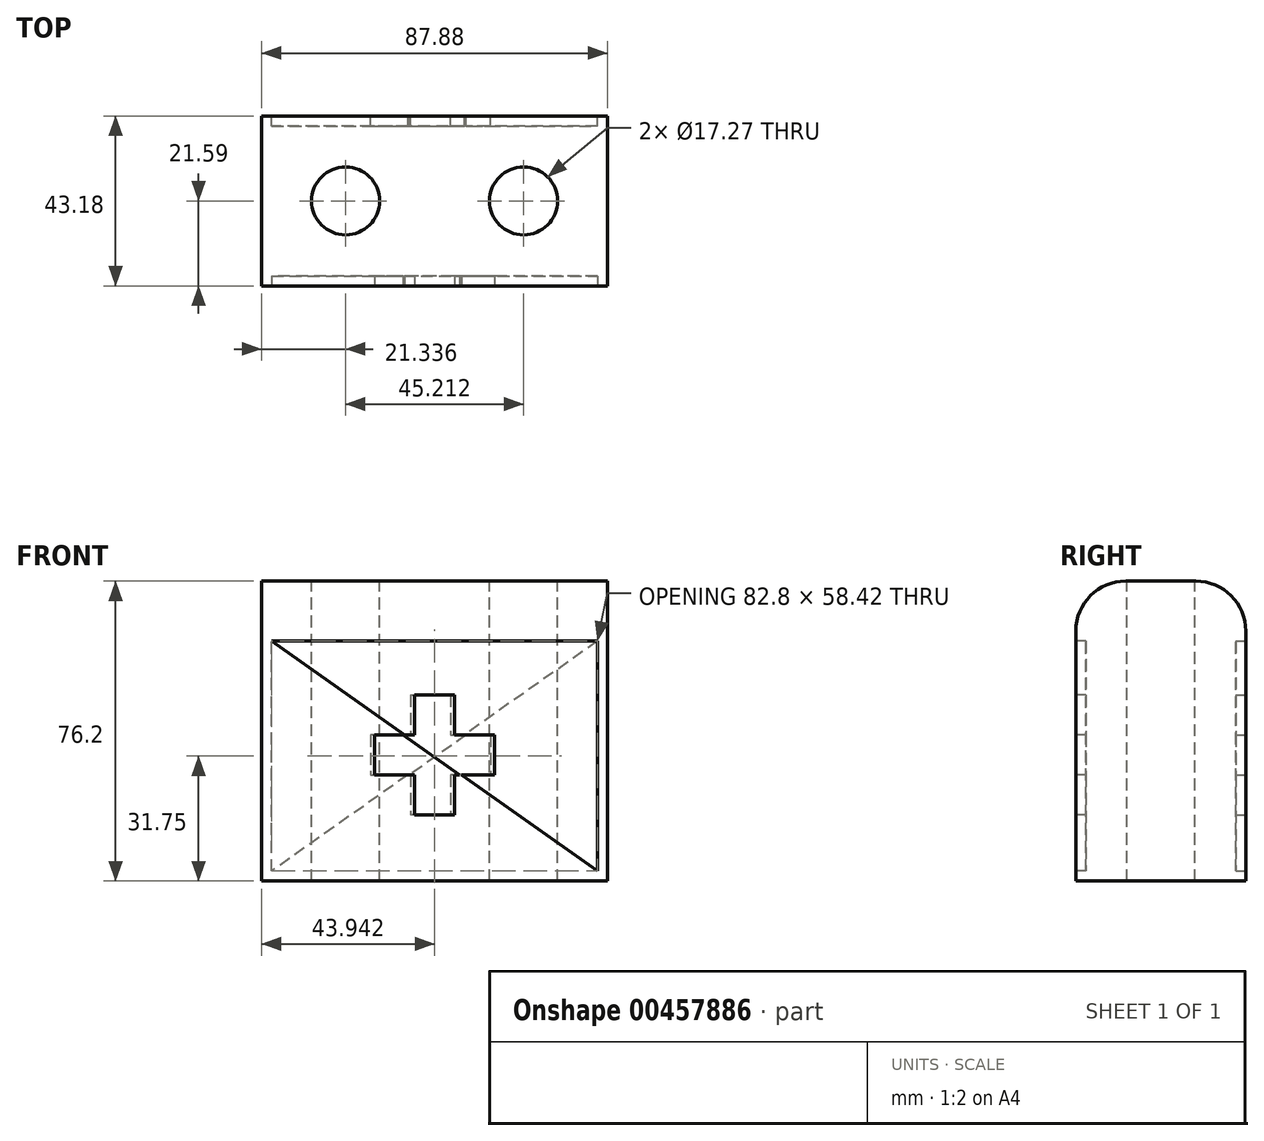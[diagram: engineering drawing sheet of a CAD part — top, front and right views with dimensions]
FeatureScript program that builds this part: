
annotation { "Feature Type Name" : "Feature", "Feature Type Description" : "" }
export const myFeature = defineFeature(function(context is Context, id is Id, definition is map)
    precondition{}
    {
        {
            var Q0;
            Q0=qCreatedBy(makeId("Front.planeOp"),FACE);
            var sketch = newSketch(context, id + "F0", { "sketchPlane" : qUnion([Q0])});
            skLineSegment(sketch, "E0.bottom", {"start": v(0, 0) * mm, "end": v(87.88, 0) * mm});
            skLineSegment(sketch, "E0.top", {"start": v(0, 76.2) * mm, "end": v(87.88, 76.2) * mm});
            skLineSegment(sketch, "E0.left", {"start": v(0, 0) * mm, "end": v(0, 76.2) * mm});
            skLineSegment(sketch, "E0.right", {"start": v(87.88, 0) * mm, "end": v(87.88, 76.2) * mm});
            skSolve(sketch);
        }
        {
            var Q0;
            Q0=makeQuery(id+"F0.imprint","IMPRINT",FACE,{"disambiguationData":[TD([[makeQuery(id+"F0.imprint","IMPRINT",EDGE,{"derivedFrom":sQuery(id+"F0.wireOp",EDGE,"E0.bottom")}),1.0]])]});
            extrude(context, id + "F1", {"entities" : qUnion([Q0]), "depth" : 43.18 * mm, "offsetDistance" : 25.4 * mm});
        }
        {
            var Q0;
            Q0=makeQuery(id+"F1.opExtrude","CAP_EDGE",EDGE,{"disambiguationData":[OSD([sQuery(id+"F0.wireOp",EDGE,"E0.top")])],"isStart":false});
            var Q1;
            Q1=makeQuery(id+"F1.opExtrude","CAP_EDGE",EDGE,{"disambiguationData":[OSD([sQuery(id+"F0.wireOp",EDGE,"E0.top")])],"isStart":true});
            fillet(context, id + "F2", {"entities" : qUnion([Q0, Q1]), "radius" : 12.7 * mm, "tangentPropagation" : true, "allowEdgeOverflow" : false});
        }
        {
            var Q0;
            Q0=makeQuery(id+"F1.opExtrude","CAP_FACE",FACE,{"disambiguationData":[OSD([sQuery(id+"F0.wireOp",EDGE,"E0.bottom"),sQuery(id+"F0.wireOp",EDGE,"E0.top"),sQuery(id+"F0.wireOp",EDGE,"E0.left"),sQuery(id+"F0.wireOp",EDGE,"E0.right")])],"isStart":false});
            var sketch = newSketch(context, id + "F3", { "sketchPlane" : qUnion([Q0])});
            skLineSegment(sketch, "E1", {"start": v(43.94, 63.5) * mm, "end": v(43.94, 0) * mm, "construction": true});
            skLineSegment(sketch, "E2", {"start": v(0, 31.75) * mm, "end": v(87.88, 31.75) * mm, "construction": true});
            skLineSegment(sketch, "E3", {"start": v(43.94, 47.28) * mm, "end": v(38.86, 47.28) * mm});
            skLineSegment(sketch, "E4", {"start": v(38.86, 47.28) * mm, "end": v(38.86, 37.12) * mm});
            skLineSegment(sketch, "E5", {"start": v(38.86, 37.12) * mm, "end": v(28.7, 37.12) * mm});
            skLineSegment(sketch, "E6", {"start": v(28.7, 37.12) * mm, "end": v(28.7, 26.96) * mm});
            skLineSegment(sketch, "E7", {"start": v(28.7, 26.96) * mm, "end": v(38.86, 26.96) * mm});
            skLineSegment(sketch, "E8", {"start": v(38.86, 26.96) * mm, "end": v(38.86, 16.8) * mm});
            skLineSegment(sketch, "E9", {"start": v(38.86, 16.8) * mm, "end": v(43.94, 16.8) * mm});
            skLineSegment(sketch, "E10.MirrorCS", {"start": v(49.02, 16.8) * mm, "end": v(43.94, 16.8) * mm});
            skLineSegment(sketch, "E11.MirrorCS", {"start": v(49.02, 26.96) * mm, "end": v(49.02, 16.8) * mm});
            skLineSegment(sketch, "E12.MirrorCS", {"start": v(59.18, 26.96) * mm, "end": v(49.02, 26.96) * mm});
            skLineSegment(sketch, "E13.MirrorCS", {"start": v(59.18, 37.12) * mm, "end": v(59.18, 26.96) * mm});
            skLineSegment(sketch, "E14.MirrorCS", {"start": v(49.02, 37.12) * mm, "end": v(59.18, 37.12) * mm});
            skLineSegment(sketch, "E15.MirrorCS", {"start": v(49.02, 47.28) * mm, "end": v(49.02, 37.12) * mm});
            skLineSegment(sketch, "E16.MirrorCS", {"start": v(43.94, 47.28) * mm, "end": v(49.02, 47.28) * mm});
            skLineSegment(sketch, "E17.0", {"start": v(85.34, 2.54) * mm, "end": v(85.34, 60.96) * mm});
            skLineSegment(sketch, "E17.1", {"start": v(2.54, 2.54) * mm, "end": v(85.34, 2.54) * mm});
            skLineSegment(sketch, "E17.2", {"start": v(2.54, 60.96) * mm, "end": v(2.54, 2.54) * mm});
            skLineSegment(sketch, "E17.3", {"start": v(85.34, 60.96) * mm, "end": v(2.54, 60.96) * mm});
            skLineSegment(sketch, "E18", {"start": v(2.54, 60.96) * mm, "end": v(85.34, 2.54) * mm});
            skLineSegment(sketch, "E19", {"start": v(35.89, 37.12) * mm, "end": v(50.29, 26.96) * mm});
            skSolve(sketch);
        }
        {
            var Q0;
            Q0=makeQuery(id+"F3.imprint","IMPRINT",FACE,{"disambiguationData":[TD([[makeQuery(id+"F3.imprint","IMPRINT",EDGE,{"derivedFrom":sQuery(id+"F3.wireOp",EDGE,"E3")}),-1.0]])]});
            extrude(context, id + "F4", {"entities" : qUnion([Q0]), "operationType" : NewBodyOperationType.REMOVE, "oppositeDirection" : true, "depth" : 2.54 * mm, "offsetDistance" : 25.4 * mm});
        }
        {
            var Q0;
            {var subQ0=sQuery(id+"F3.wireOp",EDGE,"E6");Q0=makeQuery(id+"F3.imprint","IMPRINT",FACE,{"disambiguationData":[TD([[makeQuery(id+"F3.imprint","IMPRINT",EDGE,{"derivedFrom":subQ0}),1.0]])]});}
            extrude(context, id + "F5", {"entities" : qUnion([Q0]), "operationType" : NewBodyOperationType.REMOVE, "oppositeDirection" : true, "depth" : 2.54 * mm, "offsetDistance" : 25.4 * mm});
        }
        {
            var Q0;
            Q0=makeQuery(id+"F1.opExtrude","CAP_FACE",FACE,{"disambiguationData":[OSD([sQuery(id+"F0.wireOp",EDGE,"E0.bottom"),sQuery(id+"F0.wireOp",EDGE,"E0.top"),sQuery(id+"F0.wireOp",EDGE,"E0.left"),sQuery(id+"F0.wireOp",EDGE,"E0.right")])],"isStart":true});
            var sketch = newSketch(context, id + "F6", { "sketchPlane" : qUnion([Q0])});
            skLineSegment(sketch, "E20", {"start": v(-42.92, 64.5) * mm, "end": v(-42.92, 1) * mm, "construction": true});
            skLineSegment(sketch, "E21", {"start": v(-86.86, 32.75) * mm, "end": v(1.02, 32.75) * mm, "construction": true});
            skLineSegment(sketch, "E22", {"start": v(-42.92, 47.28) * mm, "end": v(-48, 47.28) * mm});
            skLineSegment(sketch, "E23", {"start": v(-48, 47.28) * mm, "end": v(-48, 37.12) * mm});
            skLineSegment(sketch, "E24", {"start": v(-48, 37.12) * mm, "end": v(-58.16, 37.12) * mm});
            skLineSegment(sketch, "E25", {"start": v(-58.16, 37.12) * mm, "end": v(-58.16, 26.96) * mm});
            skLineSegment(sketch, "E26", {"start": v(-58.16, 26.96) * mm, "end": v(-48, 26.96) * mm});
            skLineSegment(sketch, "E27", {"start": v(-48, 26.96) * mm, "end": v(-48, 16.8) * mm});
            skLineSegment(sketch, "E28", {"start": v(-48, 16.8) * mm, "end": v(-42.92, 16.8) * mm});
            skLineSegment(sketch, "E29.MirrorCS", {"start": v(-37.84, 16.8) * mm, "end": v(-42.92, 16.8) * mm});
            skLineSegment(sketch, "E30.MirrorCS", {"start": v(-37.84, 26.96) * mm, "end": v(-37.84, 16.8) * mm});
            skLineSegment(sketch, "E31.MirrorCS", {"start": v(-27.68, 26.96) * mm, "end": v(-37.84, 26.96) * mm});
            skLineSegment(sketch, "E32.MirrorCS", {"start": v(-27.68, 37.12) * mm, "end": v(-27.68, 26.96) * mm});
            skLineSegment(sketch, "E33.MirrorCS", {"start": v(-37.84, 37.12) * mm, "end": v(-27.68, 37.12) * mm});
            skLineSegment(sketch, "E34.MirrorCS", {"start": v(-37.84, 47.28) * mm, "end": v(-37.84, 37.12) * mm});
            skLineSegment(sketch, "E35.MirrorCS", {"start": v(-42.92, 47.28) * mm, "end": v(-37.84, 47.28) * mm});
            skLineSegment(sketch, "E36.0", {"start": v(-2.54, 2.54) * mm, "end": v(-2.54, 60.96) * mm});
            skLineSegment(sketch, "E36.1", {"start": v(-85.34, 2.54) * mm, "end": v(-2.54, 2.54) * mm});
            skLineSegment(sketch, "E36.2", {"start": v(-85.34, 60.96) * mm, "end": v(-85.34, 2.54) * mm});
            skLineSegment(sketch, "E36.3", {"start": v(-2.54, 60.96) * mm, "end": v(-85.34, 60.96) * mm});
            skLineSegment(sketch, "E37", {"start": v(-85.34, 60.96) * mm, "end": v(-2.54, 2.54) * mm});
            skLineSegment(sketch, "E38", {"start": v(-52, 37.12) * mm, "end": v(-37.6, 26.96) * mm});
            skSolve(sketch);
        }
        {
            var Q0;
            Q0=makeQuery(id+"F6.imprint","IMPRINT",FACE,{"disambiguationData":[TD([[makeQuery(id+"F6.imprint","IMPRINT",EDGE,{"derivedFrom":sQuery(id+"F6.wireOp",EDGE,"E22")}),-1.0]])]});
            var Q1;
            {var subQ0=sQuery(id+"F6.wireOp",EDGE,"E25");Q1=makeQuery(id+"F6.imprint","IMPRINT",FACE,{"disambiguationData":[TD([[makeQuery(id+"F6.imprint","IMPRINT",EDGE,{"derivedFrom":subQ0}),1.0]])]});}
            extrude(context, id + "F7", {"entities" : qUnion([Q0, Q1]), "operationType" : NewBodyOperationType.REMOVE, "oppositeDirection" : true, "depth" : 2.54 * mm, "offsetDistance" : 25.4 * mm});
        }
        {
            var Q0;
            Q0=makeQuery(id+"F1.opExtrude","SWEPT_FACE",FACE,{"disambiguationData":[OSD([sQuery(id+"F0.wireOp",EDGE,"E0.top")])]});
            var sketch = newSketch(context, id + "F8", { "sketchPlane" : qUnion([Q0])});
            skLineSegment(sketch, "E39", {"start": v(0, -21.59) * mm, "end": v(87.88, -21.59) * mm, "construction": true});
            skCircle(sketch, "E40", {"center": v(21.34, -21.6) * mm, "radius": 8.64 * mm});
            skCircle(sketch, "E41", {"center": v(66.55, -21.59) * mm, "radius": 8.64 * mm});
            skSolve(sketch);
        }
        {
            var Q0;
            Q0=makeQuery(id+"F8.imprint","IMPRINT",FACE,{"disambiguationData":[TD([[makeQuery(id+"F8.imprint","IMPRINT",EDGE,{"derivedFrom":sQuery(id+"F8.wireOp",EDGE,"E40")}),1.0]])]});
            var Q1;
            Q1=makeQuery(id+"F8.imprint","IMPRINT",FACE,{"disambiguationData":[TD([[makeQuery(id+"F8.imprint","IMPRINT",EDGE,{"derivedFrom":sQuery(id+"F8.wireOp",EDGE,"E41")}),1.0]])]});
            extrude(context, id + "F9", {"entities" : qUnion([Q0, Q1]), "operationType" : NewBodyOperationType.REMOVE, "endBound" : BoundingType.THROUGH_ALL, "oppositeDirection" : true, "depth" : 25.4 * mm, "offsetDistance" : 25.4 * mm});
        }
    });
